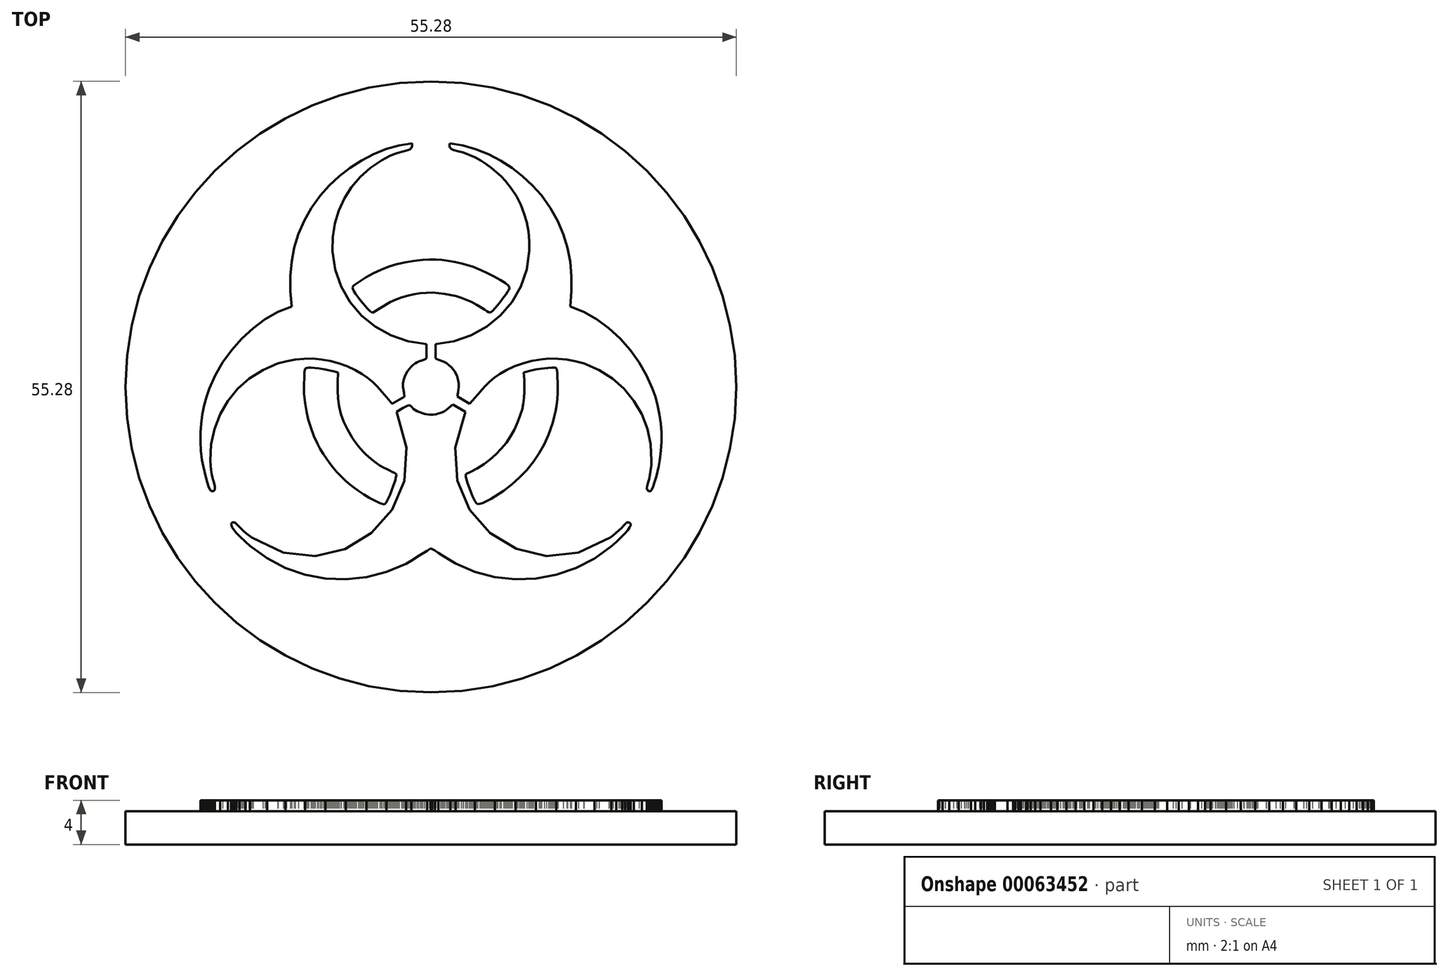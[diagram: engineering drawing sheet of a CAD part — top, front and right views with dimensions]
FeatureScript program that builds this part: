
annotation { "Feature Type Name" : "Feature", "Feature Type Description" : "" }
export const myFeature = defineFeature(function(context is Context, id is Id, definition is map)
    precondition{}
    {
        {
            var Q0;
            Q0=qCreatedBy(makeId("Top.planeOp"),FACE);
            var sketch = newSketch(context, id + "F0", { "sketchPlane" : qUnion([Q0])});
            skLineSegment(sketch, "E0", {"start": v(-12.6, 4.98) * mm, "end": v(-13.83, 4.48) * mm});
            skLineSegment(sketch, "E1", {"start": v(-13.83, 4.48) * mm, "end": v(-15, 3.8) * mm});
            skLineSegment(sketch, "E2", {"start": v(-15, 3.8) * mm, "end": v(-16.1, 3) * mm});
            skLineSegment(sketch, "E3", {"start": v(-16.1, 3) * mm, "end": v(-17.12, 2.07) * mm});
            skLineSegment(sketch, "E4", {"start": v(-17.12, 2.07) * mm, "end": v(-18.04, 1.03) * mm});
            skLineSegment(sketch, "E5", {"start": v(-18.04, 1.03) * mm, "end": v(-18.84, -0.08) * mm});
            skLineSegment(sketch, "E6", {"start": v(-18.84, -0.08) * mm, "end": v(-19.52, -1.25) * mm});
            skLineSegment(sketch, "E7", {"start": v(-19.52, -1.25) * mm, "end": v(-20.05, -2.46) * mm});
            skLineSegment(sketch, "E8", {"start": v(-20.05, -2.46) * mm, "end": v(-20.31, -3.24) * mm});
            skLineSegment(sketch, "E9", {"start": v(-20.31, -3.24) * mm, "end": v(-20.53, -4.04) * mm});
            skLineSegment(sketch, "E10", {"start": v(-20.53, -4.04) * mm, "end": v(-20.69, -4.83) * mm});
            skLineSegment(sketch, "E11", {"start": v(-20.69, -4.83) * mm, "end": v(-20.8, -5.64) * mm});
            skLineSegment(sketch, "E12", {"start": v(-20.8, -5.64) * mm, "end": v(-20.85, -6.45) * mm});
            skLineSegment(sketch, "E13", {"start": v(-20.85, -6.45) * mm, "end": v(-20.86, -7.26) * mm});
            skLineSegment(sketch, "E14", {"start": v(-20.86, -7.26) * mm, "end": v(-20.81, -8.08) * mm});
            skLineSegment(sketch, "E15", {"start": v(-20.81, -8.08) * mm, "end": v(-20.72, -8.9) * mm});
            skLineSegment(sketch, "E16", {"start": v(-20.72, -8.9) * mm, "end": v(-20.6, -9.49) * mm});
            skLineSegment(sketch, "E17", {"start": v(-20.6, -9.49) * mm, "end": v(-20.38, -10.44) * mm});
            skLineSegment(sketch, "E18", {"start": v(-20.38, -10.44) * mm, "end": v(-20.25, -10.92) * mm});
            skLineSegment(sketch, "E19", {"start": v(-20.25, -10.92) * mm, "end": v(-20.11, -11.33) * mm});
            skLineSegment(sketch, "E20", {"start": v(-20.11, -11.33) * mm, "end": v(-19.99, -11.62) * mm});
            skLineSegment(sketch, "E21", {"start": v(-19.99, -11.62) * mm, "end": v(-19.88, -11.74) * mm});
            skLineSegment(sketch, "E22", {"start": v(-19.88, -11.74) * mm, "end": v(-19.69, -11.74) * mm});
            skLineSegment(sketch, "E23", {"start": v(-19.69, -11.74) * mm, "end": v(-19.58, -11.65) * mm});
            skLineSegment(sketch, "E24", {"start": v(-19.58, -11.65) * mm, "end": v(-19.54, -11.5) * mm});
            skLineSegment(sketch, "E25", {"start": v(-19.54, -11.5) * mm, "end": v(-19.55, -11.32) * mm});
            skLineSegment(sketch, "E26", {"start": v(-19.55, -11.32) * mm, "end": v(-19.66, -10.93) * mm});
            skLineSegment(sketch, "E27", {"start": v(-19.66, -10.93) * mm, "end": v(-19.74, -10.64) * mm});
            skLineSegment(sketch, "E28", {"start": v(-19.74, -10.64) * mm, "end": v(-19.82, -10.22) * mm});
            skLineSegment(sketch, "E29", {"start": v(-19.82, -10.22) * mm, "end": v(-19.88, -9.82) * mm});
            skLineSegment(sketch, "E30", {"start": v(-19.88, -9.82) * mm, "end": v(-19.93, -9.41) * mm});
            skLineSegment(sketch, "E31", {"start": v(-19.93, -9.41) * mm, "end": v(-19.95, -8.98) * mm});
            skLineSegment(sketch, "E32", {"start": v(-19.95, -8.98) * mm, "end": v(-19.88, -7.51) * mm});
            skLineSegment(sketch, "E33", {"start": v(-19.88, -7.51) * mm, "end": v(-19.58, -6.1) * mm});
            skLineSegment(sketch, "E34", {"start": v(-19.58, -6.1) * mm, "end": v(-19.08, -4.79) * mm});
            skLineSegment(sketch, "E35", {"start": v(-19.08, -4.79) * mm, "end": v(-18.37, -3.57) * mm});
            skLineSegment(sketch, "E36", {"start": v(-18.37, -3.57) * mm, "end": v(-17.48, -2.48) * mm});
            skLineSegment(sketch, "E37", {"start": v(-17.48, -2.48) * mm, "end": v(-16.42, -1.54) * mm});
            skLineSegment(sketch, "E38", {"start": v(-16.42, -1.54) * mm, "end": v(-15.21, -0.77) * mm});
            skLineSegment(sketch, "E39", {"start": v(-15.21, -0.77) * mm, "end": v(-13.86, -0.2) * mm});
            skLineSegment(sketch, "E40", {"start": v(-13.86, -0.2) * mm, "end": v(-13.08, 0.02) * mm});
            skLineSegment(sketch, "E41", {"start": v(-13.08, 0.02) * mm, "end": v(-12.3, 0.17) * mm});
            skLineSegment(sketch, "E42", {"start": v(-12.3, 0.17) * mm, "end": v(-11.5, 0.24) * mm});
            skLineSegment(sketch, "E43", {"start": v(-11.5, 0.24) * mm, "end": v(-10.69, 0.25) * mm});
            skLineSegment(sketch, "E44", {"start": v(-10.69, 0.25) * mm, "end": v(-9.89, 0.18) * mm});
            skLineSegment(sketch, "E45", {"start": v(-9.89, 0.18) * mm, "end": v(-9.1, 0.04) * mm});
            skLineSegment(sketch, "E46", {"start": v(-9.1, 0.04) * mm, "end": v(-8.32, -0.17) * mm});
            skLineSegment(sketch, "E47", {"start": v(-8.32, -0.17) * mm, "end": v(-7.56, -0.45) * mm});
            skLineSegment(sketch, "E48", {"start": v(-7.56, -0.45) * mm, "end": v(-6.84, -0.79) * mm});
            skLineSegment(sketch, "E49", {"start": v(-6.84, -0.79) * mm, "end": v(-6.24, -1.13) * mm});
            skLineSegment(sketch, "E50", {"start": v(-6.24, -1.13) * mm, "end": v(-5.73, -1.49) * mm});
            skLineSegment(sketch, "E51", {"start": v(-5.73, -1.49) * mm, "end": v(-5.27, -1.87) * mm});
            skLineSegment(sketch, "E52", {"start": v(-5.27, -1.87) * mm, "end": v(-4.85, -2.28) * mm});
            skLineSegment(sketch, "E53", {"start": v(-4.85, -2.28) * mm, "end": v(-4.44, -2.74) * mm});
            skLineSegment(sketch, "E54", {"start": v(-4.44, -2.74) * mm, "end": v(-4, -3.26) * mm});
            skLineSegment(sketch, "E55", {"start": v(-4, -3.26) * mm, "end": v(-3.5, -3.84) * mm});
            skLineSegment(sketch, "E56", {"start": v(-3.5, -3.84) * mm, "end": v(-2.4, -3.19) * mm});
            skLineSegment(sketch, "E57", {"start": v(-2.4, -3.19) * mm, "end": v(-2.44, -2.82) * mm});
            skLineSegment(sketch, "E58", {"start": v(-2.44, -2.82) * mm, "end": v(-2.52, -2.3) * mm});
            skLineSegment(sketch, "E59", {"start": v(-2.52, -2.3) * mm, "end": v(-2.52, -2) * mm});
            skLineSegment(sketch, "E60", {"start": v(-2.52, -2) * mm, "end": v(-2.47, -1.66) * mm});
            skLineSegment(sketch, "E61", {"start": v(-2.47, -1.66) * mm, "end": v(-2.34, -1.29) * mm});
            skLineSegment(sketch, "E62", {"start": v(-2.34, -1.29) * mm, "end": v(-2.12, -0.89) * mm});
            skLineSegment(sketch, "E63", {"start": v(-2.12, -0.89) * mm, "end": v(-1.97, -0.68) * mm});
            skLineSegment(sketch, "E64", {"start": v(-1.97, -0.68) * mm, "end": v(-1.8, -0.5) * mm});
            skLineSegment(sketch, "E65", {"start": v(-1.8, -0.5) * mm, "end": v(-1.62, -0.32) * mm});
            skLineSegment(sketch, "E66", {"start": v(-1.62, -0.32) * mm, "end": v(-1.41, -0.17) * mm});
            skLineSegment(sketch, "E67", {"start": v(-1.41, -0.17) * mm, "end": v(-1.27, -0.09) * mm});
            skLineSegment(sketch, "E68", {"start": v(-1.27, -0.09) * mm, "end": v(-1.13, -0.02) * mm});
            skLineSegment(sketch, "E69", {"start": v(-1.13, -0.02) * mm, "end": v(-0.98, 0.04) * mm});
            skLineSegment(sketch, "E70", {"start": v(-0.98, 0.04) * mm, "end": v(-0.84, 0.08) * mm});
            skLineSegment(sketch, "E71", {"start": v(-0.84, 0.08) * mm, "end": v(-0.59, 0.17) * mm});
            skLineSegment(sketch, "E72", {"start": v(-0.59, 0.17) * mm, "end": v(-0.4, 0.25) * mm});
            skLineSegment(sketch, "E73", {"start": v(-0.4, 0.25) * mm, "end": v(-0.4, 1.56) * mm});
            skLineSegment(sketch, "E74", {"start": v(-0.4, 1.56) * mm, "end": v(-2.07, 1.82) * mm});
            skLineSegment(sketch, "E75", {"start": v(-2.07, 1.82) * mm, "end": v(-3.62, 2.35) * mm});
            skLineSegment(sketch, "E76", {"start": v(-3.62, 2.35) * mm, "end": v(-5.04, 3.14) * mm});
            skLineSegment(sketch, "E77", {"start": v(-5.04, 3.14) * mm, "end": v(-6.29, 4.15) * mm});
            skLineSegment(sketch, "E78", {"start": v(-6.29, 4.15) * mm, "end": v(-7.33, 5.37) * mm});
            skLineSegment(sketch, "E79", {"start": v(-7.33, 5.37) * mm, "end": v(-8.13, 6.76) * mm});
            skLineSegment(sketch, "E80", {"start": v(-8.13, 6.76) * mm, "end": v(-8.67, 8.3) * mm});
            skLineSegment(sketch, "E81", {"start": v(-8.67, 8.3) * mm, "end": v(-8.9, 9.99) * mm});
            skLineSegment(sketch, "E82", {"start": v(-8.9, 9.99) * mm, "end": v(-8.87, 11.26) * mm});
            skLineSegment(sketch, "E83", {"start": v(-8.87, 11.26) * mm, "end": v(-8.68, 12.48) * mm});
            skLineSegment(sketch, "E84", {"start": v(-8.68, 12.48) * mm, "end": v(-8.33, 13.64) * mm});
            skLineSegment(sketch, "E85", {"start": v(-8.33, 13.64) * mm, "end": v(-7.83, 14.74) * mm});
            skLineSegment(sketch, "E86", {"start": v(-7.83, 14.74) * mm, "end": v(-7.19, 15.76) * mm});
            skLineSegment(sketch, "E87", {"start": v(-7.19, 15.76) * mm, "end": v(-6.4, 16.68) * mm});
            skLineSegment(sketch, "E88", {"start": v(-6.4, 16.68) * mm, "end": v(-5.48, 17.5) * mm});
            skLineSegment(sketch, "E89", {"start": v(-5.48, 17.5) * mm, "end": v(-4.44, 18.21) * mm});
            skLineSegment(sketch, "E90", {"start": v(-4.44, 18.21) * mm, "end": v(-4.09, 18.4) * mm});
            skLineSegment(sketch, "E91", {"start": v(-4.09, 18.4) * mm, "end": v(-3.72, 18.58) * mm});
            skLineSegment(sketch, "E92", {"start": v(-3.72, 18.58) * mm, "end": v(-3.35, 18.74) * mm});
            skLineSegment(sketch, "E93", {"start": v(-3.35, 18.74) * mm, "end": v(-2.98, 18.88) * mm});
            skLineSegment(sketch, "E94", {"start": v(-2.98, 18.88) * mm, "end": v(-2.49, 19) * mm});
            skLineSegment(sketch, "E95", {"start": v(-2.49, 19) * mm, "end": v(-2.06, 19.11) * mm});
            skLineSegment(sketch, "E96", {"start": v(-2.06, 19.11) * mm, "end": v(-1.9, 19.2) * mm});
            skLineSegment(sketch, "E97", {"start": v(-1.9, 19.2) * mm, "end": v(-1.78, 19.31) * mm});
            skLineSegment(sketch, "E98", {"start": v(-1.78, 19.31) * mm, "end": v(-1.7, 19.48) * mm});
            skLineSegment(sketch, "E99", {"start": v(-1.7, 19.48) * mm, "end": v(-1.7, 19.72) * mm});
            skLineSegment(sketch, "E100", {"start": v(-1.7, 19.72) * mm, "end": v(-2.88, 19.53) * mm});
            skLineSegment(sketch, "E101", {"start": v(-2.88, 19.53) * mm, "end": v(-4.05, 19.2) * mm});
            skLineSegment(sketch, "E102", {"start": v(-4.05, 19.2) * mm, "end": v(-5.19, 18.75) * mm});
            skLineSegment(sketch, "E103", {"start": v(-5.19, 18.75) * mm, "end": v(-6.28, 18.18) * mm});
            skLineSegment(sketch, "E104", {"start": v(-6.28, 18.18) * mm, "end": v(-7.33, 17.51) * mm});
            skLineSegment(sketch, "E105", {"start": v(-7.33, 17.51) * mm, "end": v(-8.3, 16.75) * mm});
            skLineSegment(sketch, "E106", {"start": v(-8.3, 16.75) * mm, "end": v(-9.19, 15.92) * mm});
            skLineSegment(sketch, "E107", {"start": v(-9.19, 15.92) * mm, "end": v(-9.98, 15.03) * mm});
            skLineSegment(sketch, "E108", {"start": v(-9.98, 15.03) * mm, "end": v(-10.8, 13.9) * mm});
            skLineSegment(sketch, "E109", {"start": v(-10.8, 13.9) * mm, "end": v(-11.47, 12.72) * mm});
            skLineSegment(sketch, "E110", {"start": v(-11.47, 12.72) * mm, "end": v(-11.98, 11.52) * mm});
            skLineSegment(sketch, "E111", {"start": v(-11.98, 11.52) * mm, "end": v(-12.36, 10.29) * mm});
            skLineSegment(sketch, "E112", {"start": v(-12.36, 10.29) * mm, "end": v(-12.6, 9.02) * mm});
            skLineSegment(sketch, "E113", {"start": v(-12.6, 9.02) * mm, "end": v(-12.72, 7.7) * mm});
            skLineSegment(sketch, "E114", {"start": v(-12.72, 7.7) * mm, "end": v(-12.71, 6.36) * mm});
            skLineSegment(sketch, "E115", {"start": v(-12.71, 6.36) * mm, "end": v(-12.6, 4.98) * mm});
            skLineSegment(sketch, "E116", {"start": v(0.4, 1.56) * mm, "end": v(0.4, 0.25) * mm});
            skLineSegment(sketch, "E117", {"start": v(0.4, 0.25) * mm, "end": v(0.71, 0.13) * mm});
            skLineSegment(sketch, "E118", {"start": v(0.71, 0.13) * mm, "end": v(1.15, -0.03) * mm});
            skLineSegment(sketch, "E119", {"start": v(1.15, -0.03) * mm, "end": v(1.4, -0.16) * mm});
            skLineSegment(sketch, "E120", {"start": v(1.4, -0.16) * mm, "end": v(1.64, -0.34) * mm});
            skLineSegment(sketch, "E121", {"start": v(1.64, -0.34) * mm, "end": v(1.89, -0.57) * mm});
            skLineSegment(sketch, "E122", {"start": v(1.89, -0.57) * mm, "end": v(2.12, -0.89) * mm});
            skLineSegment(sketch, "E123", {"start": v(2.12, -0.89) * mm, "end": v(2.34, -1.3) * mm});
            skLineSegment(sketch, "E124", {"start": v(2.34, -1.3) * mm, "end": v(2.47, -1.67) * mm});
            skLineSegment(sketch, "E125", {"start": v(2.47, -1.67) * mm, "end": v(2.52, -2) * mm});
            skLineSegment(sketch, "E126", {"start": v(2.52, -2) * mm, "end": v(2.52, -2.31) * mm});
            skLineSegment(sketch, "E127", {"start": v(2.52, -2.31) * mm, "end": v(2.45, -2.82) * mm});
            skLineSegment(sketch, "E128", {"start": v(2.45, -2.82) * mm, "end": v(2.4, -3.18) * mm});
            skLineSegment(sketch, "E129", {"start": v(2.4, -3.18) * mm, "end": v(3.51, -3.83) * mm});
            skLineSegment(sketch, "E130", {"start": v(3.51, -3.83) * mm, "end": v(4, -3.25) * mm});
            skLineSegment(sketch, "E131", {"start": v(4, -3.25) * mm, "end": v(4.44, -2.74) * mm});
            skLineSegment(sketch, "E132", {"start": v(4.44, -2.74) * mm, "end": v(4.86, -2.28) * mm});
            skLineSegment(sketch, "E133", {"start": v(4.86, -2.28) * mm, "end": v(5.28, -1.87) * mm});
            skLineSegment(sketch, "E134", {"start": v(5.28, -1.87) * mm, "end": v(5.73, -1.48) * mm});
            skLineSegment(sketch, "E135", {"start": v(5.73, -1.48) * mm, "end": v(6.25, -1.13) * mm});
            skLineSegment(sketch, "E136", {"start": v(6.25, -1.13) * mm, "end": v(6.85, -0.79) * mm});
            skLineSegment(sketch, "E137", {"start": v(6.85, -0.79) * mm, "end": v(7.57, -0.45) * mm});
            skLineSegment(sketch, "E138", {"start": v(7.57, -0.45) * mm, "end": v(8.32, -0.17) * mm});
            skLineSegment(sketch, "E139", {"start": v(8.32, -0.17) * mm, "end": v(9.1, 0.04) * mm});
            skLineSegment(sketch, "E140", {"start": v(9.1, 0.04) * mm, "end": v(9.9, 0.18) * mm});
            skLineSegment(sketch, "E141", {"start": v(9.9, 0.18) * mm, "end": v(10.7, 0.25) * mm});
            skLineSegment(sketch, "E142", {"start": v(10.7, 0.25) * mm, "end": v(11.5, 0.24) * mm});
            skLineSegment(sketch, "E143", {"start": v(11.5, 0.24) * mm, "end": v(12.3, 0.17) * mm});
            skLineSegment(sketch, "E144", {"start": v(12.3, 0.17) * mm, "end": v(13.09, 0.02) * mm});
            skLineSegment(sketch, "E145", {"start": v(13.09, 0.02) * mm, "end": v(13.86, -0.2) * mm});
            skLineSegment(sketch, "E146", {"start": v(13.86, -0.2) * mm, "end": v(15.21, -0.77) * mm});
            skLineSegment(sketch, "E147", {"start": v(15.21, -0.77) * mm, "end": v(16.43, -1.54) * mm});
            skLineSegment(sketch, "E148", {"start": v(16.43, -1.54) * mm, "end": v(17.48, -2.48) * mm});
            skLineSegment(sketch, "E149", {"start": v(17.48, -2.48) * mm, "end": v(18.37, -3.57) * mm});
            skLineSegment(sketch, "E150", {"start": v(18.37, -3.57) * mm, "end": v(19.08, -4.79) * mm});
            skLineSegment(sketch, "E151", {"start": v(19.08, -4.79) * mm, "end": v(19.59, -6.1) * mm});
            skLineSegment(sketch, "E152", {"start": v(19.59, -6.1) * mm, "end": v(19.88, -7.51) * mm});
            skLineSegment(sketch, "E153", {"start": v(19.88, -7.51) * mm, "end": v(19.96, -8.98) * mm});
            skLineSegment(sketch, "E154", {"start": v(19.96, -8.98) * mm, "end": v(19.93, -9.4) * mm});
            skLineSegment(sketch, "E155", {"start": v(19.93, -9.4) * mm, "end": v(19.89, -9.8) * mm});
            skLineSegment(sketch, "E156", {"start": v(19.89, -9.8) * mm, "end": v(19.82, -10.2) * mm});
            skLineSegment(sketch, "E157", {"start": v(19.82, -10.2) * mm, "end": v(19.75, -10.62) * mm});
            skLineSegment(sketch, "E158", {"start": v(19.75, -10.62) * mm, "end": v(19.66, -10.91) * mm});
            skLineSegment(sketch, "E159", {"start": v(19.66, -10.91) * mm, "end": v(19.56, -11.31) * mm});
            skLineSegment(sketch, "E160", {"start": v(19.56, -11.31) * mm, "end": v(19.54, -11.5) * mm});
            skLineSegment(sketch, "E161", {"start": v(19.54, -11.5) * mm, "end": v(19.58, -11.65) * mm});
            skLineSegment(sketch, "E162", {"start": v(19.58, -11.65) * mm, "end": v(19.69, -11.73) * mm});
            skLineSegment(sketch, "E163", {"start": v(19.69, -11.73) * mm, "end": v(19.88, -11.74) * mm});
            skLineSegment(sketch, "E164", {"start": v(19.88, -11.74) * mm, "end": v(20, -11.62) * mm});
            skLineSegment(sketch, "E165", {"start": v(20, -11.62) * mm, "end": v(20.12, -11.33) * mm});
            skLineSegment(sketch, "E166", {"start": v(20.12, -11.33) * mm, "end": v(20.25, -10.92) * mm});
            skLineSegment(sketch, "E167", {"start": v(20.25, -10.92) * mm, "end": v(20.38, -10.44) * mm});
            skLineSegment(sketch, "E168", {"start": v(20.38, -10.44) * mm, "end": v(20.6, -9.49) * mm});
            skLineSegment(sketch, "E169", {"start": v(20.6, -9.49) * mm, "end": v(20.72, -8.9) * mm});
            skLineSegment(sketch, "E170", {"start": v(20.72, -8.9) * mm, "end": v(20.82, -8.08) * mm});
            skLineSegment(sketch, "E171", {"start": v(20.82, -8.08) * mm, "end": v(20.86, -7.26) * mm});
            skLineSegment(sketch, "E172", {"start": v(20.86, -7.26) * mm, "end": v(20.86, -6.45) * mm});
            skLineSegment(sketch, "E173", {"start": v(20.86, -6.45) * mm, "end": v(20.8, -5.64) * mm});
            skLineSegment(sketch, "E174", {"start": v(20.8, -5.64) * mm, "end": v(20.7, -4.83) * mm});
            skLineSegment(sketch, "E175", {"start": v(20.7, -4.83) * mm, "end": v(20.53, -4.04) * mm});
            skLineSegment(sketch, "E176", {"start": v(20.53, -4.04) * mm, "end": v(20.32, -3.24) * mm});
            skLineSegment(sketch, "E177", {"start": v(20.32, -3.24) * mm, "end": v(20.05, -2.46) * mm});
            skLineSegment(sketch, "E178", {"start": v(20.05, -2.46) * mm, "end": v(19.52, -1.25) * mm});
            skLineSegment(sketch, "E179", {"start": v(19.52, -1.25) * mm, "end": v(18.84, -0.08) * mm});
            skLineSegment(sketch, "E180", {"start": v(18.84, -0.08) * mm, "end": v(18.04, 1.03) * mm});
            skLineSegment(sketch, "E181", {"start": v(18.04, 1.03) * mm, "end": v(17.12, 2.07) * mm});
            skLineSegment(sketch, "E182", {"start": v(17.12, 2.07) * mm, "end": v(16.1, 3) * mm});
            skLineSegment(sketch, "E183", {"start": v(16.1, 3) * mm, "end": v(15, 3.8) * mm});
            skLineSegment(sketch, "E184", {"start": v(15, 3.8) * mm, "end": v(13.83, 4.47) * mm});
            skLineSegment(sketch, "E185", {"start": v(13.83, 4.47) * mm, "end": v(12.6, 4.98) * mm});
            skLineSegment(sketch, "E186", {"start": v(12.6, 4.98) * mm, "end": v(12.72, 6.35) * mm});
            skLineSegment(sketch, "E187", {"start": v(12.72, 6.35) * mm, "end": v(12.72, 7.7) * mm});
            skLineSegment(sketch, "E188", {"start": v(12.72, 7.7) * mm, "end": v(12.6, 9) * mm});
            skLineSegment(sketch, "E189", {"start": v(12.6, 9) * mm, "end": v(12.36, 10.28) * mm});
            skLineSegment(sketch, "E190", {"start": v(12.36, 10.28) * mm, "end": v(11.99, 11.52) * mm});
            skLineSegment(sketch, "E191", {"start": v(11.99, 11.52) * mm, "end": v(11.47, 12.72) * mm});
            skLineSegment(sketch, "E192", {"start": v(11.47, 12.72) * mm, "end": v(10.81, 13.88) * mm});
            skLineSegment(sketch, "E193", {"start": v(10.81, 13.88) * mm, "end": v(10, 15.01) * mm});
            skLineSegment(sketch, "E194", {"start": v(10, 15.01) * mm, "end": v(9.2, 15.91) * mm});
            skLineSegment(sketch, "E195", {"start": v(9.2, 15.91) * mm, "end": v(8.31, 16.75) * mm});
            skLineSegment(sketch, "E196", {"start": v(8.31, 16.75) * mm, "end": v(7.34, 17.5) * mm});
            skLineSegment(sketch, "E197", {"start": v(7.34, 17.5) * mm, "end": v(6.3, 18.17) * mm});
            skLineSegment(sketch, "E198", {"start": v(6.3, 18.17) * mm, "end": v(5.22, 18.73) * mm});
            skLineSegment(sketch, "E199", {"start": v(5.22, 18.73) * mm, "end": v(4.08, 19.19) * mm});
            skLineSegment(sketch, "E200", {"start": v(4.08, 19.19) * mm, "end": v(2.91, 19.52) * mm});
            skLineSegment(sketch, "E201", {"start": v(2.91, 19.52) * mm, "end": v(1.72, 19.71) * mm});
            skLineSegment(sketch, "E202", {"start": v(1.72, 19.71) * mm, "end": v(1.67, 19.51) * mm});
            skLineSegment(sketch, "E203", {"start": v(1.67, 19.51) * mm, "end": v(1.72, 19.35) * mm});
            skLineSegment(sketch, "E204", {"start": v(1.72, 19.35) * mm, "end": v(1.85, 19.23) * mm});
            skLineSegment(sketch, "E205", {"start": v(1.85, 19.23) * mm, "end": v(2.05, 19.13) * mm});
            skLineSegment(sketch, "E206", {"start": v(2.05, 19.13) * mm, "end": v(2.51, 19) * mm});
            skLineSegment(sketch, "E207", {"start": v(2.51, 19) * mm, "end": v(2.94, 18.9) * mm});
            skLineSegment(sketch, "E208", {"start": v(2.94, 18.9) * mm, "end": v(3.48, 18.69) * mm});
            skLineSegment(sketch, "E209", {"start": v(3.48, 18.69) * mm, "end": v(4, 18.44) * mm});
            skLineSegment(sketch, "E210", {"start": v(4, 18.44) * mm, "end": v(4.52, 18.17) * mm});
            skLineSegment(sketch, "E211", {"start": v(4.52, 18.17) * mm, "end": v(5, 17.85) * mm});
            skLineSegment(sketch, "E212", {"start": v(5, 17.85) * mm, "end": v(5.48, 17.5) * mm});
            skLineSegment(sketch, "E213", {"start": v(5.48, 17.5) * mm, "end": v(5.93, 17.14) * mm});
            skLineSegment(sketch, "E214", {"start": v(5.93, 17.14) * mm, "end": v(6.35, 16.74) * mm});
            skLineSegment(sketch, "E215", {"start": v(6.35, 16.74) * mm, "end": v(6.74, 16.32) * mm});
            skLineSegment(sketch, "E216", {"start": v(6.74, 16.32) * mm, "end": v(7.28, 15.63) * mm});
            skLineSegment(sketch, "E217", {"start": v(7.28, 15.63) * mm, "end": v(7.74, 14.91) * mm});
            skLineSegment(sketch, "E218", {"start": v(7.74, 14.91) * mm, "end": v(8.13, 14.16) * mm});
            skLineSegment(sketch, "E219", {"start": v(8.13, 14.16) * mm, "end": v(8.43, 13.38) * mm});
            skLineSegment(sketch, "E220", {"start": v(8.43, 13.38) * mm, "end": v(8.67, 12.57) * mm});
            skLineSegment(sketch, "E221", {"start": v(8.67, 12.57) * mm, "end": v(8.82, 11.73) * mm});
            skLineSegment(sketch, "E222", {"start": v(8.82, 11.73) * mm, "end": v(8.9, 10.88) * mm});
            skLineSegment(sketch, "E223", {"start": v(8.9, 10.88) * mm, "end": v(8.9, 10.01) * mm});
            skLineSegment(sketch, "E224", {"start": v(8.9, 10.01) * mm, "end": v(8.68, 8.33) * mm});
            skLineSegment(sketch, "E225", {"start": v(8.68, 8.33) * mm, "end": v(8.14, 6.78) * mm});
            skLineSegment(sketch, "E226", {"start": v(8.14, 6.78) * mm, "end": v(7.34, 5.38) * mm});
            skLineSegment(sketch, "E227", {"start": v(7.34, 5.38) * mm, "end": v(6.3, 4.16) * mm});
            skLineSegment(sketch, "E228", {"start": v(6.3, 4.16) * mm, "end": v(5.05, 3.14) * mm});
            skLineSegment(sketch, "E229", {"start": v(5.05, 3.14) * mm, "end": v(3.63, 2.35) * mm});
            skLineSegment(sketch, "E230", {"start": v(3.63, 2.35) * mm, "end": v(2.07, 1.82) * mm});
            skLineSegment(sketch, "E231", {"start": v(2.07, 1.82) * mm, "end": v(0.4, 1.56) * mm});
            skLineSegment(sketch, "E232", {"start": v(-3.12, -4.56) * mm, "end": v(-2.2, -7.81) * mm});
            skLineSegment(sketch, "E233", {"start": v(-2.2, -7.81) * mm, "end": v(-2.41, -10.82) * mm});
            skLineSegment(sketch, "E234", {"start": v(-2.41, -10.82) * mm, "end": v(-3.53, -13.43) * mm});
            skLineSegment(sketch, "E235", {"start": v(-3.53, -13.43) * mm, "end": v(-5.38, -15.53) * mm});
            skLineSegment(sketch, "E236", {"start": v(-5.38, -15.53) * mm, "end": v(-7.76, -16.97) * mm});
            skLineSegment(sketch, "E237", {"start": v(-7.76, -16.97) * mm, "end": v(-10.48, -17.6) * mm});
            skLineSegment(sketch, "E238", {"start": v(-10.48, -17.6) * mm, "end": v(-13.36, -17.3) * mm});
            skLineSegment(sketch, "E239", {"start": v(-13.36, -17.3) * mm, "end": v(-16.2, -15.94) * mm});
            skLineSegment(sketch, "E240", {"start": v(-16.2, -15.94) * mm, "end": v(-16.47, -15.74) * mm});
            skLineSegment(sketch, "E241", {"start": v(-16.47, -15.74) * mm, "end": v(-16.72, -15.54) * mm});
            skLineSegment(sketch, "E242", {"start": v(-16.72, -15.54) * mm, "end": v(-16.96, -15.33) * mm});
            skLineSegment(sketch, "E243", {"start": v(-16.96, -15.33) * mm, "end": v(-17.2, -15.1) * mm});
            skLineSegment(sketch, "E244", {"start": v(-17.2, -15.1) * mm, "end": v(-17.44, -14.85) * mm});
            skLineSegment(sketch, "E245", {"start": v(-17.44, -14.85) * mm, "end": v(-17.67, -14.62) * mm});
            skLineSegment(sketch, "E246", {"start": v(-17.67, -14.62) * mm, "end": v(-17.73, -14.6) * mm});
            skLineSegment(sketch, "E247", {"start": v(-17.73, -14.6) * mm, "end": v(-17.8, -14.57) * mm});
            skLineSegment(sketch, "E248", {"start": v(-17.8, -14.57) * mm, "end": v(-17.87, -14.57) * mm});
            skLineSegment(sketch, "E249", {"start": v(-17.87, -14.57) * mm, "end": v(-17.94, -14.58) * mm});
            skLineSegment(sketch, "E250", {"start": v(-17.94, -14.58) * mm, "end": v(-18, -14.6) * mm});
            skLineSegment(sketch, "E251", {"start": v(-18, -14.6) * mm, "end": v(-18.05, -14.65) * mm});
            skLineSegment(sketch, "E252", {"start": v(-18.05, -14.65) * mm, "end": v(-18.07, -14.71) * mm});
            skLineSegment(sketch, "E253", {"start": v(-18.07, -14.71) * mm, "end": v(-18.07, -14.8) * mm});
            skLineSegment(sketch, "E254", {"start": v(-18.07, -14.8) * mm, "end": v(-17.99, -15) * mm});
            skLineSegment(sketch, "E255", {"start": v(-17.99, -15) * mm, "end": v(-17.82, -15.25) * mm});
            skLineSegment(sketch, "E256", {"start": v(-17.82, -15.25) * mm, "end": v(-17.6, -15.51) * mm});
            skLineSegment(sketch, "E257", {"start": v(-17.6, -15.51) * mm, "end": v(-17.34, -15.8) * mm});
            skLineSegment(sketch, "E258", {"start": v(-17.34, -15.8) * mm, "end": v(-16.8, -16.31) * mm});
            skLineSegment(sketch, "E259", {"start": v(-16.8, -16.31) * mm, "end": v(-16.36, -16.69) * mm});
            skLineSegment(sketch, "E260", {"start": v(-16.36, -16.69) * mm, "end": v(-14.83, -17.82) * mm});
            skLineSegment(sketch, "E261", {"start": v(-14.83, -17.82) * mm, "end": v(-13.16, -18.69) * mm});
            skLineSegment(sketch, "E262", {"start": v(-13.16, -18.69) * mm, "end": v(-11.39, -19.3) * mm});
            skLineSegment(sketch, "E263", {"start": v(-11.39, -19.3) * mm, "end": v(-9.56, -19.64) * mm});
            skLineSegment(sketch, "E264", {"start": v(-9.56, -19.64) * mm, "end": v(-7.7, -19.72) * mm});
            skLineSegment(sketch, "E265", {"start": v(-7.7, -19.72) * mm, "end": v(-5.83, -19.52) * mm});
            skLineSegment(sketch, "E266", {"start": v(-5.83, -19.52) * mm, "end": v(-4.01, -19.06) * mm});
            skLineSegment(sketch, "E267", {"start": v(-4.01, -19.06) * mm, "end": v(-2.26, -18.31) * mm});
            skLineSegment(sketch, "E268", {"start": v(-2.26, -18.31) * mm, "end": v(-1.78, -18.03) * mm});
            skLineSegment(sketch, "E269", {"start": v(-1.78, -18.03) * mm, "end": v(-1.04, -17.56) * mm});
            skLineSegment(sketch, "E270", {"start": v(-1.04, -17.56) * mm, "end": v(-0.35, -17.12) * mm});
            skLineSegment(sketch, "E271", {"start": v(-0.35, -17.12) * mm, "end": v(0, -16.93) * mm});
            skLineSegment(sketch, "E272", {"start": v(0, -16.93) * mm, "end": v(0.12, -16.98) * mm});
            skLineSegment(sketch, "E273", {"start": v(0.12, -16.98) * mm, "end": v(0.35, -17.12) * mm});
            skLineSegment(sketch, "E274", {"start": v(0.35, -17.12) * mm, "end": v(0.67, -17.31) * mm});
            skLineSegment(sketch, "E275", {"start": v(0.67, -17.31) * mm, "end": v(1.03, -17.54) * mm});
            skLineSegment(sketch, "E276", {"start": v(1.03, -17.54) * mm, "end": v(1.75, -18) * mm});
            skLineSegment(sketch, "E277", {"start": v(1.75, -18) * mm, "end": v(2.23, -18.3) * mm});
            skLineSegment(sketch, "E278", {"start": v(2.23, -18.3) * mm, "end": v(3.97, -19.04) * mm});
            skLineSegment(sketch, "E279", {"start": v(3.97, -19.04) * mm, "end": v(5.8, -19.52) * mm});
            skLineSegment(sketch, "E280", {"start": v(5.8, -19.52) * mm, "end": v(7.65, -19.71) * mm});
            skLineSegment(sketch, "E281", {"start": v(7.65, -19.71) * mm, "end": v(9.52, -19.64) * mm});
            skLineSegment(sketch, "E282", {"start": v(9.52, -19.64) * mm, "end": v(11.35, -19.3) * mm});
            skLineSegment(sketch, "E283", {"start": v(11.35, -19.3) * mm, "end": v(13.13, -18.7) * mm});
            skLineSegment(sketch, "E284", {"start": v(13.13, -18.7) * mm, "end": v(14.8, -17.84) * mm});
            skLineSegment(sketch, "E285", {"start": v(14.8, -17.84) * mm, "end": v(16.34, -16.72) * mm});
            skLineSegment(sketch, "E286", {"start": v(16.34, -16.72) * mm, "end": v(16.76, -16.34) * mm});
            skLineSegment(sketch, "E287", {"start": v(16.76, -16.34) * mm, "end": v(17.31, -15.81) * mm});
            skLineSegment(sketch, "E288", {"start": v(17.31, -15.81) * mm, "end": v(17.58, -15.54) * mm});
            skLineSegment(sketch, "E289", {"start": v(17.58, -15.54) * mm, "end": v(17.8, -15.27) * mm});
            skLineSegment(sketch, "E290", {"start": v(17.8, -15.27) * mm, "end": v(17.98, -15.02) * mm});
            skLineSegment(sketch, "E291", {"start": v(17.98, -15.02) * mm, "end": v(18.07, -14.83) * mm});
            skLineSegment(sketch, "E292", {"start": v(18.07, -14.83) * mm, "end": v(18.07, -14.74) * mm});
            skLineSegment(sketch, "E293", {"start": v(18.07, -14.74) * mm, "end": v(18.05, -14.67) * mm});
            skLineSegment(sketch, "E294", {"start": v(18.05, -14.67) * mm, "end": v(18.01, -14.62) * mm});
            skLineSegment(sketch, "E295", {"start": v(18.01, -14.62) * mm, "end": v(17.96, -14.58) * mm});
            skLineSegment(sketch, "E296", {"start": v(17.96, -14.58) * mm, "end": v(17.9, -14.57) * mm});
            skLineSegment(sketch, "E297", {"start": v(17.9, -14.57) * mm, "end": v(17.82, -14.56) * mm});
            skLineSegment(sketch, "E298", {"start": v(17.82, -14.56) * mm, "end": v(17.76, -14.58) * mm});
            skLineSegment(sketch, "E299", {"start": v(17.76, -14.58) * mm, "end": v(17.7, -14.6) * mm});
            skLineSegment(sketch, "E300", {"start": v(17.7, -14.6) * mm, "end": v(17.47, -14.82) * mm});
            skLineSegment(sketch, "E301", {"start": v(17.47, -14.82) * mm, "end": v(17.24, -15.08) * mm});
            skLineSegment(sketch, "E302", {"start": v(17.24, -15.08) * mm, "end": v(17, -15.3) * mm});
            skLineSegment(sketch, "E303", {"start": v(17, -15.3) * mm, "end": v(16.74, -15.52) * mm});
            skLineSegment(sketch, "E304", {"start": v(16.74, -15.52) * mm, "end": v(16.49, -15.73) * mm});
            skLineSegment(sketch, "E305", {"start": v(16.49, -15.73) * mm, "end": v(16.22, -15.93) * mm});
            skLineSegment(sketch, "E306", {"start": v(16.22, -15.93) * mm, "end": v(13.36, -17.3) * mm});
            skLineSegment(sketch, "E307", {"start": v(13.36, -17.3) * mm, "end": v(10.47, -17.6) * mm});
            skLineSegment(sketch, "E308", {"start": v(10.47, -17.6) * mm, "end": v(7.74, -16.95) * mm});
            skLineSegment(sketch, "E309", {"start": v(7.74, -16.95) * mm, "end": v(5.35, -15.5) * mm});
            skLineSegment(sketch, "E310", {"start": v(5.35, -15.5) * mm, "end": v(3.51, -13.4) * mm});
            skLineSegment(sketch, "E311", {"start": v(3.51, -13.4) * mm, "end": v(2.4, -10.79) * mm});
            skLineSegment(sketch, "E312", {"start": v(2.4, -10.79) * mm, "end": v(2.2, -7.8) * mm});
            skLineSegment(sketch, "E313", {"start": v(2.2, -7.8) * mm, "end": v(3.12, -4.56) * mm});
            skLineSegment(sketch, "E314", {"start": v(3.12, -4.56) * mm, "end": v(1.99, -3.9) * mm});
            skLineSegment(sketch, "E315", {"start": v(1.99, -3.9) * mm, "end": v(1.78, -4.06) * mm});
            skLineSegment(sketch, "E316", {"start": v(1.78, -4.06) * mm, "end": v(1.54, -4.27) * mm});
            skLineSegment(sketch, "E317", {"start": v(1.54, -4.27) * mm, "end": v(1.4, -4.38) * mm});
            skLineSegment(sketch, "E318", {"start": v(1.4, -4.38) * mm, "end": v(1.24, -4.49) * mm});
            skLineSegment(sketch, "E319", {"start": v(1.24, -4.49) * mm, "end": v(1.06, -4.59) * mm});
            skLineSegment(sketch, "E320", {"start": v(1.06, -4.59) * mm, "end": v(0.85, -4.67) * mm});
            skLineSegment(sketch, "E321", {"start": v(0.85, -4.67) * mm, "end": v(0.65, -4.73) * mm});
            skLineSegment(sketch, "E322", {"start": v(0.65, -4.73) * mm, "end": v(0.45, -4.78) * mm});
            skLineSegment(sketch, "E323", {"start": v(0.45, -4.78) * mm, "end": v(0.25, -4.8) * mm});
            skLineSegment(sketch, "E324", {"start": v(0.25, -4.8) * mm, "end": v(0.05, -4.82) * mm});
            skLineSegment(sketch, "E325", {"start": v(0.05, -4.82) * mm, "end": v(-0.16, -4.82) * mm});
            skLineSegment(sketch, "E326", {"start": v(-0.16, -4.82) * mm, "end": v(-0.36, -4.8) * mm});
            skLineSegment(sketch, "E327", {"start": v(-0.36, -4.8) * mm, "end": v(-0.56, -4.76) * mm});
            skLineSegment(sketch, "E328", {"start": v(-0.56, -4.76) * mm, "end": v(-0.77, -4.7) * mm});
            skLineSegment(sketch, "E329", {"start": v(-0.77, -4.7) * mm, "end": v(-1.27, -4.5) * mm});
            skLineSegment(sketch, "E330", {"start": v(-1.27, -4.5) * mm, "end": v(-1.57, -4.3) * mm});
            skLineSegment(sketch, "E331", {"start": v(-1.57, -4.3) * mm, "end": v(-1.73, -4.13) * mm});
            skLineSegment(sketch, "E332", {"start": v(-1.73, -4.13) * mm, "end": v(-1.84, -4.01) * mm});
            skLineSegment(sketch, "E333", {"start": v(-1.84, -4.01) * mm, "end": v(-1.95, -3.98) * mm});
            skLineSegment(sketch, "E334", {"start": v(-1.95, -3.98) * mm, "end": v(-2.15, -4.04) * mm});
            skLineSegment(sketch, "E335", {"start": v(-2.15, -4.04) * mm, "end": v(-2.52, -4.23) * mm});
            skLineSegment(sketch, "E336", {"start": v(-2.52, -4.23) * mm, "end": v(-3.12, -4.56) * mm});
            skLineSegment(sketch, "E337", {"start": v(-4.2, -12.95) * mm, "end": v(-4.07, -12.79) * mm});
            skLineSegment(sketch, "E338", {"start": v(-4.07, -12.79) * mm, "end": v(-3.9, -12.49) * mm});
            skLineSegment(sketch, "E339", {"start": v(-3.9, -12.49) * mm, "end": v(-3.72, -12.1) * mm});
            skLineSegment(sketch, "E340", {"start": v(-3.72, -12.1) * mm, "end": v(-3.54, -11.65) * mm});
            skLineSegment(sketch, "E341", {"start": v(-3.54, -11.65) * mm, "end": v(-3.38, -11.2) * mm});
            skLineSegment(sketch, "E342", {"start": v(-3.38, -11.2) * mm, "end": v(-3.24, -10.78) * mm});
            skLineSegment(sketch, "E343", {"start": v(-3.24, -10.78) * mm, "end": v(-3.15, -10.44) * mm});
            skLineSegment(sketch, "E344", {"start": v(-3.15, -10.44) * mm, "end": v(-3.12, -10.21) * mm});
            skLineSegment(sketch, "E345", {"start": v(-3.12, -10.21) * mm, "end": v(-3.3, -10.1) * mm});
            skLineSegment(sketch, "E346", {"start": v(-3.3, -10.1) * mm, "end": v(-3.51, -9.98) * mm});
            skLineSegment(sketch, "E347", {"start": v(-3.51, -9.98) * mm, "end": v(-3.74, -9.88) * mm});
            skLineSegment(sketch, "E348", {"start": v(-3.74, -9.88) * mm, "end": v(-4, -9.76) * mm});
            skLineSegment(sketch, "E349", {"start": v(-4, -9.76) * mm, "end": v(-4.3, -9.6) * mm});
            skLineSegment(sketch, "E350", {"start": v(-4.3, -9.6) * mm, "end": v(-4.62, -9.41) * mm});
            skLineSegment(sketch, "E351", {"start": v(-4.62, -9.41) * mm, "end": v(-4.99, -9.16) * mm});
            skLineSegment(sketch, "E352", {"start": v(-4.99, -9.16) * mm, "end": v(-5.4, -8.83) * mm});
            skLineSegment(sketch, "E353", {"start": v(-5.4, -8.83) * mm, "end": v(-5.65, -8.62) * mm});
            skLineSegment(sketch, "E354", {"start": v(-5.65, -8.62) * mm, "end": v(-5.9, -8.4) * mm});
            skLineSegment(sketch, "E355", {"start": v(-5.9, -8.4) * mm, "end": v(-6.12, -8.17) * mm});
            skLineSegment(sketch, "E356", {"start": v(-6.12, -8.17) * mm, "end": v(-6.34, -7.93) * mm});
            skLineSegment(sketch, "E357", {"start": v(-6.34, -7.93) * mm, "end": v(-6.55, -7.69) * mm});
            skLineSegment(sketch, "E358", {"start": v(-6.55, -7.69) * mm, "end": v(-6.75, -7.43) * mm});
            skLineSegment(sketch, "E359", {"start": v(-6.75, -7.43) * mm, "end": v(-6.95, -7.17) * mm});
            skLineSegment(sketch, "E360", {"start": v(-6.95, -7.17) * mm, "end": v(-7.13, -6.9) * mm});
            skLineSegment(sketch, "E361", {"start": v(-7.13, -6.9) * mm, "end": v(-7.56, -6.16) * mm});
            skLineSegment(sketch, "E362", {"start": v(-7.56, -6.16) * mm, "end": v(-7.9, -5.46) * mm});
            skLineSegment(sketch, "E363", {"start": v(-7.9, -5.46) * mm, "end": v(-8.14, -4.76) * mm});
            skLineSegment(sketch, "E364", {"start": v(-8.14, -4.76) * mm, "end": v(-8.3, -4.07) * mm});
            skLineSegment(sketch, "E365", {"start": v(-8.3, -4.07) * mm, "end": v(-8.4, -3.36) * mm});
            skLineSegment(sketch, "E366", {"start": v(-8.4, -3.36) * mm, "end": v(-8.45, -2.63) * mm});
            skLineSegment(sketch, "E367", {"start": v(-8.45, -2.63) * mm, "end": v(-8.44, -1.85) * mm});
            skLineSegment(sketch, "E368", {"start": v(-8.44, -1.85) * mm, "end": v(-8.4, -1.01) * mm});
            skLineSegment(sketch, "E369", {"start": v(-8.4, -1.01) * mm, "end": v(-8.73, -0.91) * mm});
            skLineSegment(sketch, "E370", {"start": v(-8.73, -0.91) * mm, "end": v(-9.04, -0.84) * mm});
            skLineSegment(sketch, "E371", {"start": v(-9.04, -0.84) * mm, "end": v(-9.33, -0.77) * mm});
            skLineSegment(sketch, "E372", {"start": v(-9.33, -0.77) * mm, "end": v(-9.61, -0.72) * mm});
            skLineSegment(sketch, "E373", {"start": v(-9.61, -0.72) * mm, "end": v(-10.2, -0.64) * mm});
            skLineSegment(sketch, "E374", {"start": v(-10.2, -0.64) * mm, "end": v(-10.85, -0.57) * mm});
            skLineSegment(sketch, "E375", {"start": v(-10.85, -0.57) * mm, "end": v(-11.08, -0.56) * mm});
            skLineSegment(sketch, "E376", {"start": v(-11.08, -0.56) * mm, "end": v(-11.24, -0.58) * mm});
            skLineSegment(sketch, "E377", {"start": v(-11.24, -0.58) * mm, "end": v(-11.34, -0.63) * mm});
            skLineSegment(sketch, "E378", {"start": v(-11.34, -0.63) * mm, "end": v(-11.4, -0.72) * mm});
            skLineSegment(sketch, "E379", {"start": v(-11.4, -0.72) * mm, "end": v(-11.44, -0.99) * mm});
            skLineSegment(sketch, "E380", {"start": v(-11.44, -0.99) * mm, "end": v(-11.46, -1.4) * mm});
            skLineSegment(sketch, "E381", {"start": v(-11.46, -1.4) * mm, "end": v(-11.5, -2.16) * mm});
            skLineSegment(sketch, "E382", {"start": v(-11.5, -2.16) * mm, "end": v(-11.48, -2.94) * mm});
            skLineSegment(sketch, "E383", {"start": v(-11.48, -2.94) * mm, "end": v(-11.4, -3.72) * mm});
            skLineSegment(sketch, "E384", {"start": v(-11.4, -3.72) * mm, "end": v(-11.27, -4.5) * mm});
            skLineSegment(sketch, "E385", {"start": v(-11.27, -4.5) * mm, "end": v(-11.1, -5.27) * mm});
            skLineSegment(sketch, "E386", {"start": v(-11.1, -5.27) * mm, "end": v(-10.86, -6.02) * mm});
            skLineSegment(sketch, "E387", {"start": v(-10.86, -6.02) * mm, "end": v(-10.59, -6.75) * mm});
            skLineSegment(sketch, "E388", {"start": v(-10.59, -6.75) * mm, "end": v(-10.27, -7.44) * mm});
            skLineSegment(sketch, "E389", {"start": v(-10.27, -7.44) * mm, "end": v(-10, -7.92) * mm});
            skLineSegment(sketch, "E390", {"start": v(-10, -7.92) * mm, "end": v(-9.74, -8.37) * mm});
            skLineSegment(sketch, "E391", {"start": v(-9.74, -8.37) * mm, "end": v(-9.46, -8.8) * mm});
            skLineSegment(sketch, "E392", {"start": v(-9.46, -8.8) * mm, "end": v(-9.17, -9.2) * mm});
            skLineSegment(sketch, "E393", {"start": v(-9.17, -9.2) * mm, "end": v(-8.85, -9.6) * mm});
            skLineSegment(sketch, "E394", {"start": v(-8.85, -9.6) * mm, "end": v(-8.52, -9.98) * mm});
            skLineSegment(sketch, "E395", {"start": v(-8.52, -9.98) * mm, "end": v(-8.16, -10.36) * mm});
            skLineSegment(sketch, "E396", {"start": v(-8.16, -10.36) * mm, "end": v(-7.77, -10.75) * mm});
            skLineSegment(sketch, "E397", {"start": v(-7.77, -10.75) * mm, "end": v(-7.44, -11.04) * mm});
            skLineSegment(sketch, "E398", {"start": v(-7.44, -11.04) * mm, "end": v(-7.03, -11.36) * mm});
            skLineSegment(sketch, "E399", {"start": v(-7.03, -11.36) * mm, "end": v(-6.57, -11.7) * mm});
            skLineSegment(sketch, "E400", {"start": v(-6.57, -11.7) * mm, "end": v(-6.08, -12.03) * mm});
            skLineSegment(sketch, "E401", {"start": v(-6.08, -12.03) * mm, "end": v(-5.57, -12.34) * mm});
            skLineSegment(sketch, "E402", {"start": v(-5.57, -12.34) * mm, "end": v(-5.08, -12.61) * mm});
            skLineSegment(sketch, "E403", {"start": v(-5.08, -12.61) * mm, "end": v(-4.61, -12.82) * mm});
            skLineSegment(sketch, "E404", {"start": v(-4.61, -12.82) * mm, "end": v(-4.2, -12.95) * mm});
            skLineSegment(sketch, "E405", {"start": v(-0.74, 9.18) * mm, "end": v(-1.53, 9.1) * mm});
            skLineSegment(sketch, "E406", {"start": v(-1.53, 9.1) * mm, "end": v(-2.3, 8.97) * mm});
            skLineSegment(sketch, "E407", {"start": v(-2.3, 8.97) * mm, "end": v(-3.06, 8.8) * mm});
            skLineSegment(sketch, "E408", {"start": v(-3.06, 8.8) * mm, "end": v(-3.79, 8.57) * mm});
            skLineSegment(sketch, "E409", {"start": v(-3.79, 8.57) * mm, "end": v(-4.5, 8.3) * mm});
            skLineSegment(sketch, "E410", {"start": v(-4.5, 8.3) * mm, "end": v(-5.2, 7.97) * mm});
            skLineSegment(sketch, "E411", {"start": v(-5.2, 7.97) * mm, "end": v(-5.89, 7.59) * mm});
            skLineSegment(sketch, "E412", {"start": v(-5.89, 7.59) * mm, "end": v(-6.56, 7.16) * mm});
            skLineSegment(sketch, "E413", {"start": v(-6.56, 7.16) * mm, "end": v(-6.77, 7.02) * mm});
            skLineSegment(sketch, "E414", {"start": v(-6.77, 7.02) * mm, "end": v(-6.93, 6.91) * mm});
            skLineSegment(sketch, "E415", {"start": v(-6.93, 6.91) * mm, "end": v(-7.04, 6.82) * mm});
            skLineSegment(sketch, "E416", {"start": v(-7.04, 6.82) * mm, "end": v(-7.1, 6.7) * mm});
            skLineSegment(sketch, "E417", {"start": v(-7.1, 6.7) * mm, "end": v(-7.07, 6.57) * mm});
            skLineSegment(sketch, "E418", {"start": v(-7.07, 6.57) * mm, "end": v(-6.98, 6.37) * mm});
            skLineSegment(sketch, "E419", {"start": v(-6.98, 6.37) * mm, "end": v(-6.8, 6.1) * mm});
            skLineSegment(sketch, "E420", {"start": v(-6.8, 6.1) * mm, "end": v(-6.54, 5.72) * mm});
            skLineSegment(sketch, "E421", {"start": v(-6.54, 5.72) * mm, "end": v(-6.3, 5.42) * mm});
            skLineSegment(sketch, "E422", {"start": v(-6.3, 5.42) * mm, "end": v(-5.93, 4.98) * mm});
            skLineSegment(sketch, "E423", {"start": v(-5.93, 4.98) * mm, "end": v(-5.73, 4.76) * mm});
            skLineSegment(sketch, "E424", {"start": v(-5.73, 4.76) * mm, "end": v(-5.54, 4.58) * mm});
            skLineSegment(sketch, "E425", {"start": v(-5.54, 4.58) * mm, "end": v(-5.4, 4.45) * mm});
            skLineSegment(sketch, "E426", {"start": v(-5.4, 4.45) * mm, "end": v(-5.3, 4.4) * mm});
            skLineSegment(sketch, "E427", {"start": v(-5.3, 4.4) * mm, "end": v(-3.68, 5.37) * mm});
            skLineSegment(sketch, "E428", {"start": v(-3.68, 5.37) * mm, "end": v(-3.17, 5.6) * mm});
            skLineSegment(sketch, "E429", {"start": v(-3.17, 5.6) * mm, "end": v(-2.64, 5.78) * mm});
            skLineSegment(sketch, "E430", {"start": v(-2.64, 5.78) * mm, "end": v(-2.1, 5.94) * mm});
            skLineSegment(sketch, "E431", {"start": v(-2.1, 5.94) * mm, "end": v(-1.53, 6.07) * mm});
            skLineSegment(sketch, "E432", {"start": v(-1.53, 6.07) * mm, "end": v(-0.97, 6.16) * mm});
            skLineSegment(sketch, "E433", {"start": v(-0.97, 6.16) * mm, "end": v(-0.4, 6.2) * mm});
            skLineSegment(sketch, "E434", {"start": v(-0.4, 6.2) * mm, "end": v(0.16, 6.22) * mm});
            skLineSegment(sketch, "E435", {"start": v(0.16, 6.22) * mm, "end": v(0.72, 6.18) * mm});
            skLineSegment(sketch, "E436", {"start": v(0.72, 6.18) * mm, "end": v(1.25, 6.1) * mm});
            skLineSegment(sketch, "E437", {"start": v(1.25, 6.1) * mm, "end": v(1.77, 6.02) * mm});
            skLineSegment(sketch, "E438", {"start": v(1.77, 6.02) * mm, "end": v(2.26, 5.9) * mm});
            skLineSegment(sketch, "E439", {"start": v(2.26, 5.9) * mm, "end": v(2.75, 5.75) * mm});
            skLineSegment(sketch, "E440", {"start": v(2.75, 5.75) * mm, "end": v(3.22, 5.58) * mm});
            skLineSegment(sketch, "E441", {"start": v(3.22, 5.58) * mm, "end": v(3.69, 5.37) * mm});
            skLineSegment(sketch, "E442", {"start": v(3.69, 5.37) * mm, "end": v(4.15, 5.13) * mm});
            skLineSegment(sketch, "E443", {"start": v(4.15, 5.13) * mm, "end": v(4.61, 4.85) * mm});
            skLineSegment(sketch, "E444", {"start": v(4.61, 4.85) * mm, "end": v(4.87, 4.67) * mm});
            skLineSegment(sketch, "E445", {"start": v(4.87, 4.67) * mm, "end": v(5.07, 4.54) * mm});
            skLineSegment(sketch, "E446", {"start": v(5.07, 4.54) * mm, "end": v(5.22, 4.45) * mm});
            skLineSegment(sketch, "E447", {"start": v(5.22, 4.45) * mm, "end": v(5.34, 4.43) * mm});
            skLineSegment(sketch, "E448", {"start": v(5.34, 4.43) * mm, "end": v(5.46, 4.47) * mm});
            skLineSegment(sketch, "E449", {"start": v(5.46, 4.47) * mm, "end": v(5.6, 4.59) * mm});
            skLineSegment(sketch, "E450", {"start": v(5.6, 4.59) * mm, "end": v(5.78, 4.8) * mm});
            skLineSegment(sketch, "E451", {"start": v(5.78, 4.8) * mm, "end": v(6.03, 5.09) * mm});
            skLineSegment(sketch, "E452", {"start": v(6.03, 5.09) * mm, "end": v(6.29, 5.4) * mm});
            skLineSegment(sketch, "E453", {"start": v(6.29, 5.4) * mm, "end": v(6.63, 5.85) * mm});
            skLineSegment(sketch, "E454", {"start": v(6.63, 5.85) * mm, "end": v(6.8, 6.08) * mm});
            skLineSegment(sketch, "E455", {"start": v(6.8, 6.08) * mm, "end": v(6.94, 6.3) * mm});
            skLineSegment(sketch, "E456", {"start": v(6.94, 6.3) * mm, "end": v(7.06, 6.48) * mm});
            skLineSegment(sketch, "E457", {"start": v(7.06, 6.48) * mm, "end": v(7.12, 6.63) * mm});
            skLineSegment(sketch, "E458", {"start": v(7.12, 6.63) * mm, "end": v(7.04, 6.82) * mm});
            skLineSegment(sketch, "E459", {"start": v(7.04, 6.82) * mm, "end": v(6.73, 7.08) * mm});
            skLineSegment(sketch, "E460", {"start": v(6.73, 7.08) * mm, "end": v(6.26, 7.37) * mm});
            skLineSegment(sketch, "E461", {"start": v(6.26, 7.37) * mm, "end": v(5.7, 7.68) * mm});
            skLineSegment(sketch, "E462", {"start": v(5.7, 7.68) * mm, "end": v(5.12, 7.98) * mm});
            skLineSegment(sketch, "E463", {"start": v(5.12, 7.98) * mm, "end": v(4.57, 8.23) * mm});
            skLineSegment(sketch, "E464", {"start": v(4.57, 8.23) * mm, "end": v(4.13, 8.43) * mm});
            skLineSegment(sketch, "E465", {"start": v(4.13, 8.43) * mm, "end": v(3.86, 8.54) * mm});
            skLineSegment(sketch, "E466", {"start": v(3.86, 8.54) * mm, "end": v(3.32, 8.72) * mm});
            skLineSegment(sketch, "E467", {"start": v(3.32, 8.72) * mm, "end": v(2.75, 8.87) * mm});
            skLineSegment(sketch, "E468", {"start": v(2.75, 8.87) * mm, "end": v(2.18, 9) * mm});
            skLineSegment(sketch, "E469", {"start": v(2.18, 9) * mm, "end": v(1.6, 9.1) * mm});
            skLineSegment(sketch, "E470", {"start": v(1.6, 9.1) * mm, "end": v(1, 9.17) * mm});
            skLineSegment(sketch, "E471", {"start": v(1, 9.17) * mm, "end": v(0.42, 9.2) * mm});
            skLineSegment(sketch, "E472", {"start": v(0.42, 9.2) * mm, "end": v(-0.16, 9.21) * mm});
            skLineSegment(sketch, "E473", {"start": v(-0.16, 9.21) * mm, "end": v(-0.74, 9.18) * mm});
            skLineSegment(sketch, "E474", {"start": v(8.4, -1.01) * mm, "end": v(8.44, -1.65) * mm});
            skLineSegment(sketch, "E475", {"start": v(8.44, -1.65) * mm, "end": v(8.46, -2.23) * mm});
            skLineSegment(sketch, "E476", {"start": v(8.46, -2.23) * mm, "end": v(8.46, -2.77) * mm});
            skLineSegment(sketch, "E477", {"start": v(8.46, -2.77) * mm, "end": v(8.43, -3.29) * mm});
            skLineSegment(sketch, "E478", {"start": v(8.43, -3.29) * mm, "end": v(8.36, -3.8) * mm});
            skLineSegment(sketch, "E479", {"start": v(8.36, -3.8) * mm, "end": v(8.25, -4.33) * mm});
            skLineSegment(sketch, "E480", {"start": v(8.25, -4.33) * mm, "end": v(8.09, -4.89) * mm});
            skLineSegment(sketch, "E481", {"start": v(8.09, -4.89) * mm, "end": v(7.86, -5.5) * mm});
            skLineSegment(sketch, "E482", {"start": v(7.86, -5.5) * mm, "end": v(7.57, -6.15) * mm});
            skLineSegment(sketch, "E483", {"start": v(7.57, -6.15) * mm, "end": v(7.22, -6.77) * mm});
            skLineSegment(sketch, "E484", {"start": v(7.22, -6.77) * mm, "end": v(6.82, -7.35) * mm});
            skLineSegment(sketch, "E485", {"start": v(6.82, -7.35) * mm, "end": v(6.38, -7.9) * mm});
            skLineSegment(sketch, "E486", {"start": v(6.38, -7.9) * mm, "end": v(5.89, -8.4) * mm});
            skLineSegment(sketch, "E487", {"start": v(5.89, -8.4) * mm, "end": v(5.36, -8.87) * mm});
            skLineSegment(sketch, "E488", {"start": v(5.36, -8.87) * mm, "end": v(4.8, -9.3) * mm});
            skLineSegment(sketch, "E489", {"start": v(4.8, -9.3) * mm, "end": v(4.2, -9.67) * mm});
            skLineSegment(sketch, "E490", {"start": v(4.2, -9.67) * mm, "end": v(3.52, -10.01) * mm});
            skLineSegment(sketch, "E491", {"start": v(3.52, -10.01) * mm, "end": v(3.2, -10.2) * mm});
            skLineSegment(sketch, "E492", {"start": v(3.2, -10.2) * mm, "end": v(3.14, -10.3) * mm});
            skLineSegment(sketch, "E493", {"start": v(3.14, -10.3) * mm, "end": v(3.15, -10.44) * mm});
            skLineSegment(sketch, "E494", {"start": v(3.15, -10.44) * mm, "end": v(3.2, -10.67) * mm});
            skLineSegment(sketch, "E495", {"start": v(3.2, -10.67) * mm, "end": v(3.31, -11) * mm});
            skLineSegment(sketch, "E496", {"start": v(3.31, -11) * mm, "end": v(3.46, -11.43) * mm});
            skLineSegment(sketch, "E497", {"start": v(3.46, -11.43) * mm, "end": v(3.66, -11.94) * mm});
            skLineSegment(sketch, "E498", {"start": v(3.66, -11.94) * mm, "end": v(3.77, -12.2) * mm});
            skLineSegment(sketch, "E499", {"start": v(3.77, -12.2) * mm, "end": v(3.88, -12.43) * mm});
            skLineSegment(sketch, "E500", {"start": v(3.88, -12.43) * mm, "end": v(4, -12.64) * mm});
            skLineSegment(sketch, "E501", {"start": v(4, -12.64) * mm, "end": v(4.1, -12.82) * mm});
            skLineSegment(sketch, "E502", {"start": v(4.1, -12.82) * mm, "end": v(4.23, -12.9) * mm});
            skLineSegment(sketch, "E503", {"start": v(4.23, -12.9) * mm, "end": v(4.42, -12.9) * mm});
            skLineSegment(sketch, "E504", {"start": v(4.42, -12.9) * mm, "end": v(4.66, -12.82) * mm});
            skLineSegment(sketch, "E505", {"start": v(4.66, -12.82) * mm, "end": v(4.93, -12.7) * mm});
            skLineSegment(sketch, "E506", {"start": v(4.93, -12.7) * mm, "end": v(5.44, -12.42) * mm});
            skLineSegment(sketch, "E507", {"start": v(5.44, -12.42) * mm, "end": v(5.79, -12.2) * mm});
            skLineSegment(sketch, "E508", {"start": v(5.79, -12.2) * mm, "end": v(6.58, -11.7) * mm});
            skLineSegment(sketch, "E509", {"start": v(6.58, -11.7) * mm, "end": v(7.32, -11.14) * mm});
            skLineSegment(sketch, "E510", {"start": v(7.32, -11.14) * mm, "end": v(8.02, -10.5) * mm});
            skLineSegment(sketch, "E511", {"start": v(8.02, -10.5) * mm, "end": v(8.68, -9.82) * mm});
            skLineSegment(sketch, "E512", {"start": v(8.68, -9.82) * mm, "end": v(9.27, -9.08) * mm});
            skLineSegment(sketch, "E513", {"start": v(9.27, -9.08) * mm, "end": v(9.8, -8.3) * mm});
            skLineSegment(sketch, "E514", {"start": v(9.8, -8.3) * mm, "end": v(10.26, -7.48) * mm});
            skLineSegment(sketch, "E515", {"start": v(10.26, -7.48) * mm, "end": v(10.64, -6.63) * mm});
            skLineSegment(sketch, "E516", {"start": v(10.64, -6.63) * mm, "end": v(10.84, -6.09) * mm});
            skLineSegment(sketch, "E517", {"start": v(10.84, -6.09) * mm, "end": v(11.02, -5.55) * mm});
            skLineSegment(sketch, "E518", {"start": v(11.02, -5.55) * mm, "end": v(11.16, -5.02) * mm});
            skLineSegment(sketch, "E519", {"start": v(11.16, -5.02) * mm, "end": v(11.28, -4.5) * mm});
            skLineSegment(sketch, "E520", {"start": v(11.28, -4.5) * mm, "end": v(11.37, -3.96) * mm});
            skLineSegment(sketch, "E521", {"start": v(11.37, -3.96) * mm, "end": v(11.43, -3.4) * mm});
            skLineSegment(sketch, "E522", {"start": v(11.43, -3.4) * mm, "end": v(11.47, -2.85) * mm});
            skLineSegment(sketch, "E523", {"start": v(11.47, -2.85) * mm, "end": v(11.48, -2.27) * mm});
            skLineSegment(sketch, "E524", {"start": v(11.48, -2.27) * mm, "end": v(11.43, -1.03) * mm});
            skLineSegment(sketch, "E525", {"start": v(11.43, -1.03) * mm, "end": v(11.41, -0.83) * mm});
            skLineSegment(sketch, "E526", {"start": v(11.41, -0.83) * mm, "end": v(11.37, -0.69) * mm});
            skLineSegment(sketch, "E527", {"start": v(11.37, -0.69) * mm, "end": v(11.3, -0.6) * mm});
            skLineSegment(sketch, "E528", {"start": v(11.3, -0.6) * mm, "end": v(11.2, -0.56) * mm});
            skLineSegment(sketch, "E529", {"start": v(11.2, -0.56) * mm, "end": v(10.94, -0.55) * mm});
            skLineSegment(sketch, "E530", {"start": v(10.94, -0.55) * mm, "end": v(10.6, -0.59) * mm});
            skLineSegment(sketch, "E531", {"start": v(10.6, -0.59) * mm, "end": v(10.01, -0.65) * mm});
            skLineSegment(sketch, "E532", {"start": v(10.01, -0.65) * mm, "end": v(9.49, -0.73) * mm});
            skLineSegment(sketch, "E533", {"start": v(9.49, -0.73) * mm, "end": v(8.97, -0.85) * mm});
            skLineSegment(sketch, "E534", {"start": v(8.97, -0.85) * mm, "end": v(8.4, -1.01) * mm});
            skCircle(sketch, "E535", {"center": v(0, -2.31) * mm, "radius": 27.64 * mm});
            skSolve(sketch);
        }
        {
            var Q0;
            Q0=makeQuery(id+"F0.imprint","IMPRINT",FACE,{"disambiguationData":[TD([[makeQuery(id+"F0.imprint","IMPRINT",EDGE,{"derivedFrom":sQuery(id+"F0.wireOp",EDGE,"E0")}),-1.0]])]});
            var Q1;
            Q1=makeQuery(id+"F0.imprint","IMPRINT",FACE,{"disambiguationData":[TD([[makeQuery(id+"F0.imprint","IMPRINT",EDGE,{"derivedFrom":sQuery(id+"F0.wireOp",EDGE,"E0")}),1.0]])]});
            var Q2;
            Q2=makeQuery(id+"F0.imprint","IMPRINT",FACE,{"disambiguationData":[TD([[makeQuery(id+"F0.imprint","IMPRINT",EDGE,{"derivedFrom":sQuery(id+"F0.wireOp",EDGE,"E405")}),1.0]])]});
            var Q3;
            Q3=makeQuery(id+"F0.imprint","IMPRINT",FACE,{"disambiguationData":[TD([[makeQuery(id+"F0.imprint","IMPRINT",EDGE,{"derivedFrom":sQuery(id+"F0.wireOp",EDGE,"E116")}),1.0]])]});
            var Q4;
            Q4=makeQuery(id+"F0.imprint","IMPRINT",FACE,{"disambiguationData":[TD([[makeQuery(id+"F0.imprint","IMPRINT",EDGE,{"derivedFrom":sQuery(id+"F0.wireOp",EDGE,"E474")}),1.0]])]});
            var Q5;
            Q5=makeQuery(id+"F0.imprint","IMPRINT",FACE,{"disambiguationData":[TD([[makeQuery(id+"F0.imprint","IMPRINT",EDGE,{"derivedFrom":sQuery(id+"F0.wireOp",EDGE,"E232")}),1.0]])]});
            var Q6;
            Q6=makeQuery(id+"F0.imprint","IMPRINT",FACE,{"disambiguationData":[TD([[makeQuery(id+"F0.imprint","IMPRINT",EDGE,{"derivedFrom":sQuery(id+"F0.wireOp",EDGE,"E337")}),1.0]])]});
            extrude(context, id + "F1", {"entities" : qUnion([Q0, Q1, Q2, Q3, Q4, Q5, Q6]), "depth" : 3 * mm});
        }
        {
            var Q0;
            Q0=makeQuery(id+"F0.imprint","IMPRINT",FACE,{"disambiguationData":[TD([[makeQuery(id+"F0.imprint","IMPRINT",EDGE,{"derivedFrom":sQuery(id+"F0.wireOp",EDGE,"E116")}),1.0]])]});
            var Q1;
            Q1=makeQuery(id+"F0.imprint","IMPRINT",FACE,{"disambiguationData":[TD([[makeQuery(id+"F0.imprint","IMPRINT",EDGE,{"derivedFrom":sQuery(id+"F0.wireOp",EDGE,"E474")}),1.0]])]});
            var Q2;
            Q2=makeQuery(id+"F0.imprint","IMPRINT",FACE,{"disambiguationData":[TD([[makeQuery(id+"F0.imprint","IMPRINT",EDGE,{"derivedFrom":sQuery(id+"F0.wireOp",EDGE,"E232")}),1.0]])]});
            var Q3;
            Q3=makeQuery(id+"F0.imprint","IMPRINT",FACE,{"disambiguationData":[TD([[makeQuery(id+"F0.imprint","IMPRINT",EDGE,{"derivedFrom":sQuery(id+"F0.wireOp",EDGE,"E337")}),1.0]])]});
            var Q4;
            Q4=makeQuery(id+"F0.imprint","IMPRINT",FACE,{"disambiguationData":[TD([[makeQuery(id+"F0.imprint","IMPRINT",EDGE,{"derivedFrom":sQuery(id+"F0.wireOp",EDGE,"E0")}),1.0]])]});
            var Q5;
            Q5=makeQuery(id+"F0.imprint","IMPRINT",FACE,{"disambiguationData":[TD([[makeQuery(id+"F0.imprint","IMPRINT",EDGE,{"derivedFrom":sQuery(id+"F0.wireOp",EDGE,"E405")}),1.0]])]});
            extrude(context, id + "F2", {"entities" : qUnion([Q0, Q1, Q2, Q3, Q4, Q5]), "operationType" : NewBodyOperationType.ADD, "depth" : 4 * mm});
        }
    });
